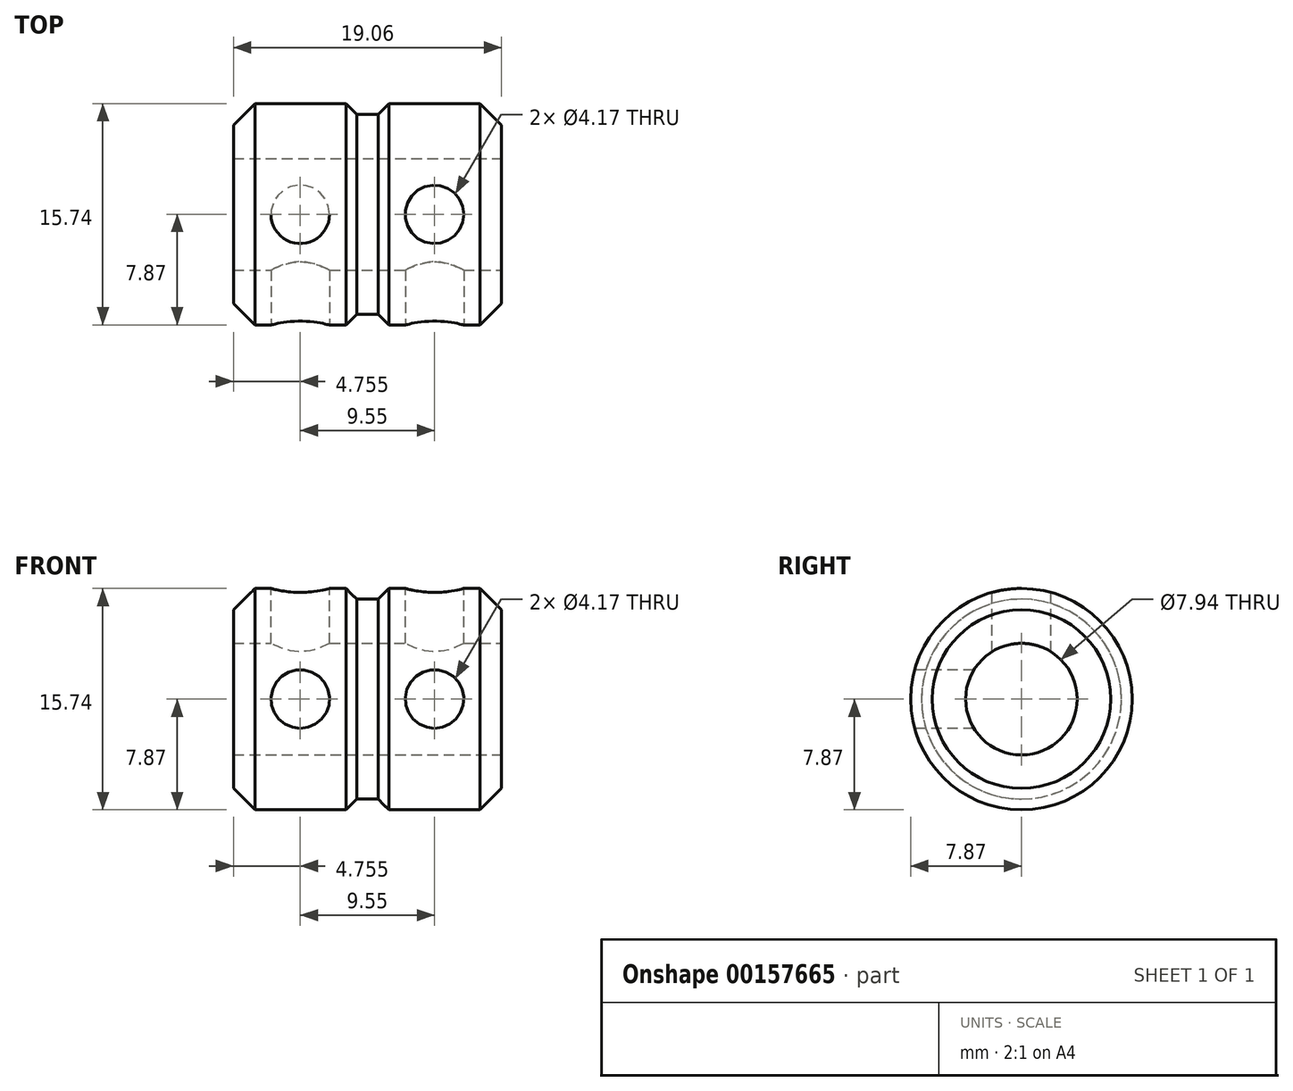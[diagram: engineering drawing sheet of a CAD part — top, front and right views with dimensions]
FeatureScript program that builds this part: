
annotation { "Feature Type Name" : "Feature", "Feature Type Description" : "" }
export const myFeature = defineFeature(function(context is Context, id is Id, definition is map)
    precondition{}
    {
        {
            var Q0;
            Q0=qCreatedBy(makeId("Right.planeOp"),FACE);
            var sketch = newSketch(context, id + "F0", { "sketchPlane" : qUnion([Q0])});
            skCircle(sketch, "E0", {"center": v(0, 0) * mm, "radius": 7.11 * mm});
            skSolve(sketch);
        }
        {
            var Q0;
            Q0=makeQuery(id+"F0.imprint","IMPRINT",FACE,{"disambiguationData":[TD([[makeQuery(id+"F0.imprint","IMPRINT",EDGE,{"derivedFrom":sQuery(id+"F0.wireOp",EDGE,"E0")}),1.0]])]});
            extrude(context, id + "F1", {"entities" : qUnion([Q0]), "depth" : 0.76 * mm, "hasSecondDirection" : true, "secondDirectionOppositeDirection" : true, "secondDirectionDepth" : 0.76 * mm});
        }
        {
            var Q0;
            Q0=makeQuery(id+"F1.opExtrude","CAP_FACE",FACE,{"disambiguationData":[OSD([sQuery(id+"F0.wireOp",EDGE,"E0")])],"isStart":false});
            var sketch = newSketch(context, id + "F2", { "sketchPlane" : qUnion([Q0])});
            skCircle(sketch, "E1", {"center": v(0, 0) * mm, "radius": 7.87 * mm});
            skSolve(sketch);
        }
        {
            var Q0;
            Q0=makeQuery(id+"F2.imprint","IMPRINT",FACE,{"disambiguationData":[TD([[makeQuery(id+"F2.imprint","IMPRINT",EDGE,{"derivedFrom":makeQuery(id+"F1.opExtrude","CAP_EDGE",EDGE,{"disambiguationData":[OSD([sQuery(id+"F0.wireOp",EDGE,"E0")])],"isStart":false})}),1.0]])]});
            var Q1;
            Q1=makeQuery(id+"F2.imprint","IMPRINT",FACE,{"disambiguationData":[TD([[makeQuery(id+"F2.imprint","IMPRINT",EDGE,{"derivedFrom":sQuery(id+"F2.wireOp",EDGE,"E1")}),1.0]])]});
            extrude(context, id + "F3", {"entities" : qUnion([Q0, Q1]), "operationType" : NewBodyOperationType.ADD, "depth" : 8.76 * mm});
        }
        {
            var Q0;
            Q0=makeQuery(id+"F1.opExtrude","CAP_FACE",FACE,{"disambiguationData":[OSD([sQuery(id+"F0.wireOp",EDGE,"E0")])],"isStart":true});
            var sketch = newSketch(context, id + "F4", { "sketchPlane" : qUnion([Q0])});
            skCircle(sketch, "E2", {"center": v(0, 0) * mm, "radius": 7.87 * mm});
            skSolve(sketch);
        }
        {
            var Q0;
            Q0=makeQuery(id+"F4.imprint","IMPRINT",FACE,{"disambiguationData":[TD([[makeQuery(id+"F4.imprint","IMPRINT",EDGE,{"derivedFrom":makeQuery(id+"F1.opExtrude","CAP_EDGE",EDGE,{"disambiguationData":[OSD([sQuery(id+"F0.wireOp",EDGE,"E0")])],"isStart":true})}),-1.0]])]});
            var Q1;
            Q1=makeQuery(id+"F4.imprint","IMPRINT",FACE,{"disambiguationData":[TD([[makeQuery(id+"F4.imprint","IMPRINT",EDGE,{"derivedFrom":sQuery(id+"F4.wireOp",EDGE,"E2")}),1.0]])]});
            extrude(context, id + "F5", {"entities" : qUnion([Q0, Q1]), "operationType" : NewBodyOperationType.ADD, "depth" : 8.76 * mm});
        }
        {
            var Q0;
            Q0=makeQuery(id+"F3.opExtrude","CAP_FACE",FACE,{"disambiguationData":[OSD([sQuery(id+"F2.wireOp",EDGE,"E1")])],"isStart":false});
            var sketch = newSketch(context, id + "F6", { "sketchPlane" : qUnion([Q0])});
            skLineSegment(sketch, "E3", {"start": v(0, 0) * mm, "end": v(0, 7.87) * mm, "construction": true});
            skLineSegment(sketch, "E4", {"start": v(0, 0) * mm, "end": v(-7.87, 0) * mm, "construction": true});
            skSolve(sketch);
        }
        {
            var Q0;
            Q0=qCreatedBy(makeId("Top.planeOp"),FACE);
            var Q1;
            Q1=sQuery(id+"F6.wireOp",VERTEX,"E3.end");
            cPlane(context, id + "F7", {"entities" : qUnion([Q0, Q1]), "cplaneType" : CPlaneType.PLANE_POINT, "offset" : 25.4 * mm, "width" : 152.4 * mm, "height" : 152.4 * mm});
        }
        {
            var Q0;
            Q0=qCreatedBy(id+"F7.planeOp",FACE);
            var sketch = newSketch(context, id + "F8", { "sketchPlane" : qUnion([Q0])});
            skLineSegment(sketch, "E5", {"start": v(0, 0) * mm, "end": v(4.78, 0) * mm, "construction": true});
            skLineSegment(sketch, "E6", {"start": v(0, 0) * mm, "end": v(-4.78, 0) * mm, "construction": true});
            skCircle(sketch, "E7", {"center": v(4.78, 0) * mm, "radius": 2.08 * mm});
            skCircle(sketch, "E8", {"center": v(-4.78, 0) * mm, "radius": 2.08 * mm});
            skSolve(sketch);
        }
        {
            var Q0;
            Q0=makeQuery(id+"F6.imprint","IMPRINT",FACE,{"disambiguationData":[TD([[makeQuery(id+"F6.imprint","IMPRINT",EDGE,{"derivedFrom":makeQuery(id+"F3.opExtrude","CAP_EDGE",EDGE,{"disambiguationData":[OSD([sQuery(id+"F2.wireOp",EDGE,"E1")])],"isStart":false})}),1.0]])]});
            var sketch = newSketch(context, id + "F9", { "sketchPlane" : qUnion([Q0])});
            skCircle(sketch, "E9", {"center": v(0, 0) * mm, "radius": 3.97 * mm});
            skSolve(sketch);
        }
        {
            var Q0;
            Q0=makeQuery(id+"F9.imprint","IMPRINT",FACE,{"disambiguationData":[TD([[makeQuery(id+"F9.imprint","IMPRINT",EDGE,{"derivedFrom":sQuery(id+"F9.wireOp",EDGE,"E9")}),1.0]])]});
            var Q1;
            Q1=sQuery(id+"F9.wireOp",EDGE,"E9");
            extrude(context, id + "F10", {"entities" : qUnion([Q0]), "operationType" : NewBodyOperationType.REMOVE, "surfaceEntities" : qUnion([Q1]), "oppositeDirection" : true, "depth" : 25.4 * mm});
        }
        {
            var Q0;
            Q0=makeQuery(id+"F8.imprint","IMPRINT",FACE,{"disambiguationData":[TD([[makeQuery(id+"F8.imprint","IMPRINT",EDGE,{"derivedFrom":sQuery(id+"F8.wireOp",EDGE,"E7")}),1.0]])]});
            var Q1;
            Q1=makeQuery(id+"F8.imprint","IMPRINT",FACE,{"disambiguationData":[TD([[makeQuery(id+"F8.imprint","IMPRINT",EDGE,{"derivedFrom":sQuery(id+"F8.wireOp",EDGE,"E8")}),1.0]])]});
            var Q2;
            Q2=sQuery(id+"F8.wireOp",EDGE,"E7");
            extrude(context, id + "F11", {"entities" : qUnion([Q0, Q1]), "operationType" : NewBodyOperationType.REMOVE, "surfaceEntities" : qUnion([Q2]), "oppositeDirection" : true, "depth" : 7.62 * mm});
        }
        {
            var Q0;
            Q0=makeQuery(id+"F6.imprint","IMPRINT",FACE,{"disambiguationData":[TD([[makeQuery(id+"F6.imprint","IMPRINT",EDGE,{"derivedFrom":makeQuery(id+"F3.opExtrude","CAP_EDGE",EDGE,{"disambiguationData":[OSD([sQuery(id+"F2.wireOp",EDGE,"E1")])],"isStart":false})}),1.0]])]});
            var sketch = newSketch(context, id + "F12", { "sketchPlane" : qUnion([Q0])});
            skLineSegment(sketch, "E10", {"start": v(0, 0) * mm, "end": v(-7.87, 0) * mm, "construction": true});
            skSolve(sketch);
        }
        {
            var Q0;
            Q0=qCreatedBy(makeId("Front.planeOp"),FACE);
            var Q1;
            Q1=sQuery(id+"F12.wireOp",VERTEX,"E10.end");
            cPlane(context, id + "F13", {"entities" : qUnion([Q0, Q1]), "cplaneType" : CPlaneType.PLANE_POINT, "offset" : 25.4 * mm, "width" : 152.4 * mm, "height" : 152.4 * mm});
        }
        {
            var Q0;
            Q0=qCreatedBy(id+"F13.planeOp",FACE);
            var sketch = newSketch(context, id + "F14", { "sketchPlane" : qUnion([Q0])});
            skLineSegment(sketch, "E11", {"start": v(0, 0) * mm, "end": v(4.78, 0) * mm, "construction": true});
            skLineSegment(sketch, "E12", {"start": v(0, 0) * mm, "end": v(-4.78, 0) * mm, "construction": true});
            skCircle(sketch, "E13", {"center": v(-4.78, 0) * mm, "radius": 2.08 * mm});
            skCircle(sketch, "E14", {"center": v(4.78, 0) * mm, "radius": 2.08 * mm});
            skSolve(sketch);
        }
        {
            var Q0;
            Q0=makeQuery(id+"F14.imprint","IMPRINT",FACE,{"disambiguationData":[TD([[makeQuery(id+"F14.imprint","IMPRINT",EDGE,{"derivedFrom":sQuery(id+"F14.wireOp",EDGE,"E14")}),1.0]])]});
            var Q1;
            Q1=makeQuery(id+"F14.imprint","IMPRINT",FACE,{"disambiguationData":[TD([[makeQuery(id+"F14.imprint","IMPRINT",EDGE,{"derivedFrom":sQuery(id+"F14.wireOp",EDGE,"E13")}),1.0]])]});
            extrude(context, id + "F15", {"entities" : qUnion([Q0, Q1]), "operationType" : NewBodyOperationType.REMOVE, "oppositeDirection" : true, "depth" : 7.87 * mm});
        }
        {
            var Q0;
            Q0=makeQuery(id+"F3.opExtrude","CAP_EDGE",EDGE,{"disambiguationData":[OSD([sQuery(id+"F2.wireOp",EDGE,"E1")])],"isStart":false});
            var Q1;
            Q1=makeQuery(id+"F5.opExtrude","CAP_EDGE",EDGE,{"disambiguationData":[OSD([sQuery(id+"F4.wireOp",EDGE,"E2")])],"isStart":false});
            chamfer(context, id + "F16", {"entities" : qUnion([Q0, Q1]), "width" : 1.52 * mm, "tangentPropagation" : true});
        }
        {
            var Q0;
            Q0=makeQuery(id+"F3.opExtrude","CAP_EDGE",EDGE,{"disambiguationData":[OSD([sQuery(id+"F2.wireOp",EDGE,"E1")])],"isStart":true});
            var Q1;
            Q1=makeQuery(id+"F5.opExtrude","CAP_EDGE",EDGE,{"disambiguationData":[OSD([sQuery(id+"F4.wireOp",EDGE,"E2")])],"isStart":true});
            chamfer(context, id + "F17", {"entities" : qUnion([Q0, Q1]), "width" : 0.76 * mm, "tangentPropagation" : true});
        }
    });
